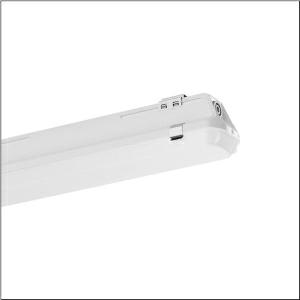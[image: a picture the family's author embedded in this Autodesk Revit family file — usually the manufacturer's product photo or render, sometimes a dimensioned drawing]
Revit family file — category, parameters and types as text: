
# Revit family: monsun_r__11_51fp10dp460h_8c07
name_source: partatom
category: Lighting Fixtures
units: mm (PartAtom-declared; Revit-internal decimal feet)

## family parameters
Cut with Voids When Loaded = No
Host = Face
Light Source = No
Part Type = Normal
Room Calculation Point = No
Round Connector Dimension = Use Diameter
Shared = No

## types (1)
- --- (1 x LED, 6050 lm, 34.6 W, 4000K)
    Apparent Load = 35 VA
    CIE Flux Codes = 47 77 93 94 100
    Color Rendering = 80
    Color Temperature = 4000K
    Default Elevation = 1800 mm
    Description = Monsun® 11, damp-proof luminaire, chain hanger, primary optical cover: enclosure, of PMMA, light emission: direct distribution, primary light characteristic: symmetric, installation type: suspended mounting, surface-mounted, horizontal mounting, vertical mounting, LED, rated luminous flux: 6.050lm, luminous efficacy: 175lm/W, light colour: 840, colour temperature: 4000K, control gear: ECG DALI, with terminal, 5-pole, max. 2.5mm², mains connection: 220..240V, AC, 50/60Hz, rated input power: 35W, luminaire housing, of glass-fibre reinforced polyester, uncoated, bright grey, incl. chain hanger, length: 1.590mm, width: 90mm, height: 88mm, clip for enclosure, of stainless steel (V2A), ceiling mounting element, of stainless steel (V2A), chain hanger, of stainless steel (V2A), protection rating (complete): IP66, insulation class (complete): insulation class I (protective earthing), certification: CE, ENEC, VDE, UKCA, protection symbol: D, impact resistance: IK04, permissible operating ambient temperature: -25..+40°C, standard: EN 50419, EN 60598-2-1, no direct snow, no direct sun, no direct rain, for indoor or canopied outdoor use, corresponds to IFS (International Featured Standards) requirements for safety and quality in the food industry, contact your sales advisor before using the luminaires in applications with unclear chemical exposure, large temperature fluctuations or condensation-forming humidity, LABS conformity tested according to VDMA 24364:2018-05, packaging unit: 1 piece
    Height = 89 mm
    Lamp = 1 x LED
    Lamp Light Flux = 6050 lm
    Lamp Power = 34.6 W
    Lamp count = 1
    Length = 1590 mm
    Luminous efficacy = 175 lm/W
    Manufacturer = Siteco
    ModVariant = No
    Model = 51FP10DP460H
    Mounting Place = Ceiling
    Mounting Type = Surface mounted
    Number of Poles = 1
    OnlyDefault = Yes
    Power Factor = 1
    Product Name = Monsun® 11
    Product group = damp-proof luminaire
    ProductGroupID = 300
    Protection Class = Protection class I
    Protection Degree = IP 66
    RLX_Detail_Level = 1
    RLX_Emergency_Light_Flux = 0 lm
    RLX_Emergency_Type = 0
    RLX_Emergency_Type_DB = No
    RlxData = <blob elided: 91913 chars, md5=891456e3>
    Socket = socket
    Standby Power = 0 W
    System Light Flux = 6050 lm
    System Power = 35 W
    Type Comments = factory setting: luminous flux: 100 % | dim-lin: 254 | 232 mA
    Type Image = l_1004748.jpg
    URL = http://relux.com
    VarID = @adj_142225
    Voltage = 0 V
    Weight = 0.00 kg
    Width = 90 mm

## geometry (parser evidence)
native form markers: Blend x4, Sweep x14
no freeform markers — native parametric forms only
